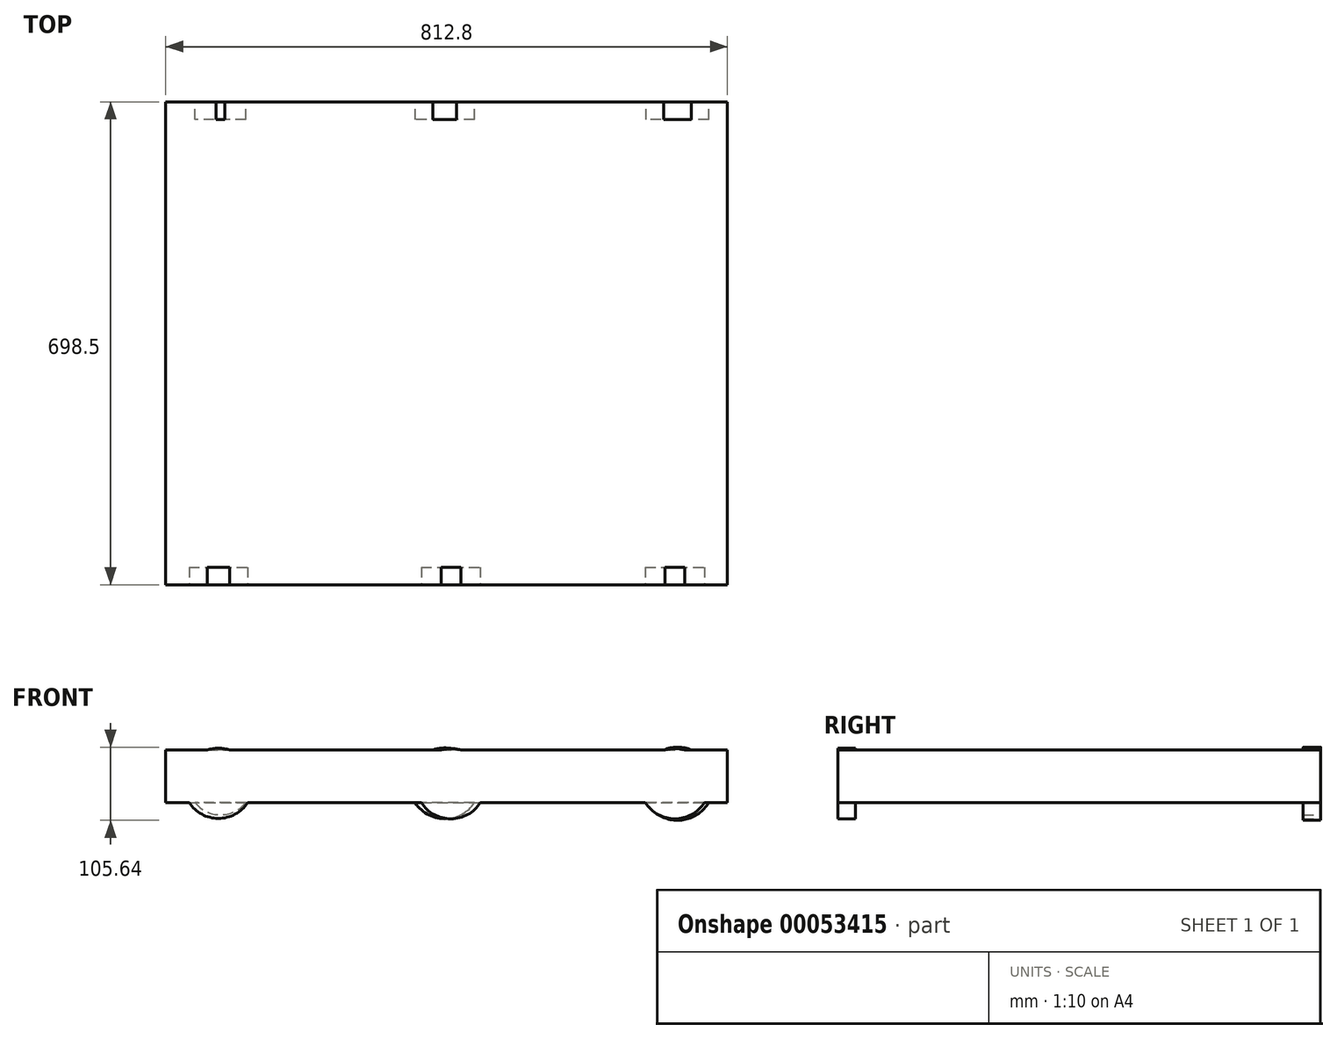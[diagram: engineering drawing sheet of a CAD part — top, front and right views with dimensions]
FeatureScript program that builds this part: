
annotation { "Feature Type Name" : "Feature", "Feature Type Description" : "" }
export const myFeature = defineFeature(function(context is Context, id is Id, definition is map)
    precondition{}
    {
        {
            var Q0;
            Q0=qCreatedBy(makeId("Front.planeOp"),FACE);
            var sketch = newSketch(context, id + "F0", { "sketchPlane" : qUnion([Q0])});
            skLineSegment(sketch, "E0.bottom", {"start": v(-274.67, -42.23) * mm, "end": v(538.13, -42.23) * mm});
            skLineSegment(sketch, "E0.top", {"start": v(-274.67, 33.97) * mm, "end": v(538.13, 33.97) * mm});
            skLineSegment(sketch, "E0.left", {"start": v(-274.67, -42.23) * mm, "end": v(-274.67, 33.97) * mm});
            skLineSegment(sketch, "E0.right", {"start": v(538.13, -42.23) * mm, "end": v(538.13, 33.97) * mm});
            skSolve(sketch);
        }
        {
            var Q0;
            Q0 = qSketchRegion(id + "F0", true);
            extrude(context, id + "F1", {"entities" : qUnion([Q0]), "depth" : 698.5 * mm});
        }
        {
            var Q0;
            Q0=makeQuery(id+"F1.opExtrude","CAP_FACE",FACE,{"disambiguationData":[OSD([sQuery(id+"F0.wireOp",EDGE,"E0.bottom"),sQuery(id+"F0.wireOp",EDGE,"E0.top"),sQuery(id+"F0.wireOp",EDGE,"E0.left"),sQuery(id+"F0.wireOp",EDGE,"E0.right")])],"isStart":false});
            var sketch = newSketch(context, id + "F2", { "sketchPlane" : qUnion([Q0])});
            skCircle(sketch, "E1", {"center": v(461.93, -14.74) * mm, "radius": 50.8 * mm});
            skCircle(sketch, "E2", {"center": v(137.78, -14.78) * mm, "radius": 50.8 * mm});
            skLineSegment(sketch, "E3", {"start": v(-274.67, -14.2) * mm, "end": v(538.13, -14.2) * mm, "construction": true});
            skCircle(sketch, "E4", {"center": v(-198.47, -14.2) * mm, "radius": 50.8 * mm});
            skSolve(sketch);
        }
        {
            var Q0;
            Q0 = qSketchRegion(id + "F2", true);
            extrude(context, id + "F3", {"entities" : qUnion([Q0]), "operationType" : NewBodyOperationType.ADD, "oppositeDirection" : true, "depth" : 25.4 * mm});
        }
        {
            var Q0;
            Q0=makeQuery(id+"F1.opExtrude","CAP_FACE",FACE,{"disambiguationData":[OSD([sQuery(id+"F0.wireOp",EDGE,"E0.bottom"),sQuery(id+"F0.wireOp",EDGE,"E0.top"),sQuery(id+"F0.wireOp",EDGE,"E0.left"),sQuery(id+"F0.wireOp",EDGE,"E0.right")])],"isStart":true});
            var sketch = newSketch(context, id + "F4", { "sketchPlane" : qUnion([Q0])});
            skCircle(sketch, "E5", {"center": v(195.58, -14.9) * mm, "radius": 50.8 * mm});
            skCircle(sketch, "E6", {"center": v(-128.57, -14.94) * mm, "radius": 50.8 * mm});
            skLineSegment(sketch, "E7", {"start": v(-541.02, -14.36) * mm, "end": v(271.78, -14.36) * mm, "construction": true});
            skCircle(sketch, "E8", {"center": v(-464.82, -14.36) * mm, "radius": 50.8 * mm});
            skSolve(sketch);
        }
        {
            var Q0;
            {var subQ0=sQuery(id+"F4.wireOp",EDGE,"E8");var subQ1=makeQuery(id+"F1.opExtrude","CAP_EDGE",EDGE,{"disambiguationData":[OSD([sQuery(id+"F0.wireOp",EDGE,"E0.top")])],"isStart":true});var subQ2=makeQuery(id+"F4.imprint","INTERSECT",VERTEX,{"disambiguationData":[OD(0.0)],"derivedFrom":[subQ1,subQ0]});Q0=makeQuery(id+"F4.imprint","IMPRINT",FACE,{"disambiguationData":[TD([[makeQuery(id+"F4.imprint","IMPRINT",EDGE,{"disambiguationData":[TD([[subQ2,-1.0]])],"derivedFrom":subQ0}),1.0]])]});}
            var sketch = newSketch(context, id + "F5", { "sketchPlane" : qUnion([Q0])});
            skCircle(sketch, "E9", {"center": v(-465.8, -14.82) * mm, "radius": 52.82 * mm});
            skCircle(sketch, "E10", {"center": v(-129, -14.23) * mm, "radius": 51.15 * mm});
            skCircle(sketch, "E11", {"center": v(195.62, -12.72) * mm, "radius": 47.1 * mm});
            skSolve(sketch);
        }
        {
            var Q0;
            Q0 = qSketchRegion(id + "F5", true);
            extrude(context, id + "F6", {"entities" : qUnion([Q0]), "operationType" : NewBodyOperationType.ADD, "oppositeDirection" : true, "depth" : 25.4 * mm});
        }
    });
